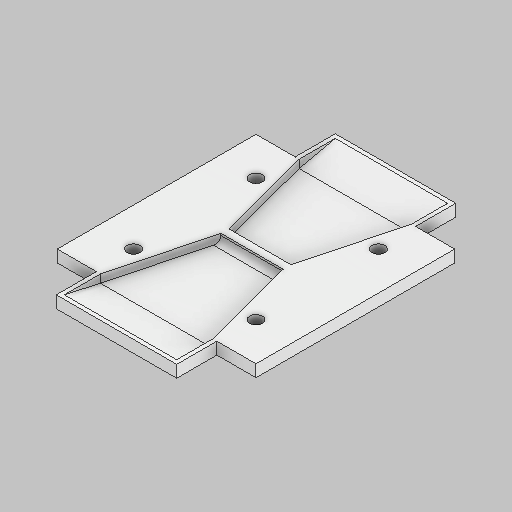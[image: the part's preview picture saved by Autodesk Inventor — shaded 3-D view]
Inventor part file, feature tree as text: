
AUTODESK INVENTOR PART (.ipt)
format: ipt  version: 2025.2 (Build 292293000, 293)  size: 319,488 bytes
history: native  units: in
note: dims shown in document units (in); Inventor stores cm internally (conversion verified against a paired STEP export)
features: sketch x6, extrude x5, fillet x2
ambient origin geometry x8: Origin, YZ Plane, XZ Plane, XY Plane, X Axis, Y Axis, Z Axis, Center Point
bodies: Solid1 (feature_tree)
feature tree (13):
  extrude  "Extrusion1"  Depth=1.9488in
  extrude  "Extrusion2"  Depth=0.126in
  extrude  "Extrusion3"  Depth=0.374in
  sketch  "Sketch4"  dims[d23=0.374in d24=0.374in]
  extrude  "Extrusion4"  Depth=0.374in
  fillet  "Face Fillet3"
  fillet  "Face Fillet4"
  extrude  "Extrusion5"  Depth=0.126in
  sketch  "Sketch1"  dims[d17=1.9488in d18=1.9488in]
  sketch  "Sketch2"  dims[d19=0.126in d20=0.126in]
  sketch  "Sketch3"  dims[d21=1.2008in d22=0.374in]
  sketch  "Sketch5"  dims[d25=0.374in d26=0.126in]
  sketch  "Sketch6"  dims[d27=0.126in d28=1.2008in d29=1.2008in d30=1.2008in d31=0.374in d32=0.374in d33=0.374in d34=0.374in d35=0.1181in d36=0.0in d37=0.5906in d38=0.3937in d39=1.1811in d40=0.5906in d41=0.3937in d42=1.1811in d43=0.1181in d44=0.0in d45=0.0394in d46=0.5512in d47=0.5512in d48=0.0394in d49=0.5512in d50=0.5512in d51=0.5906in d52=0.0787in d53=0.0in d56=0.0394in d57=0.0394in d58=0.0394in d59=0.0394in d60=0.0787in d61=0.0in d62=0.0591in d63=0.0591in d64=1.1412in d65=0.0in]
